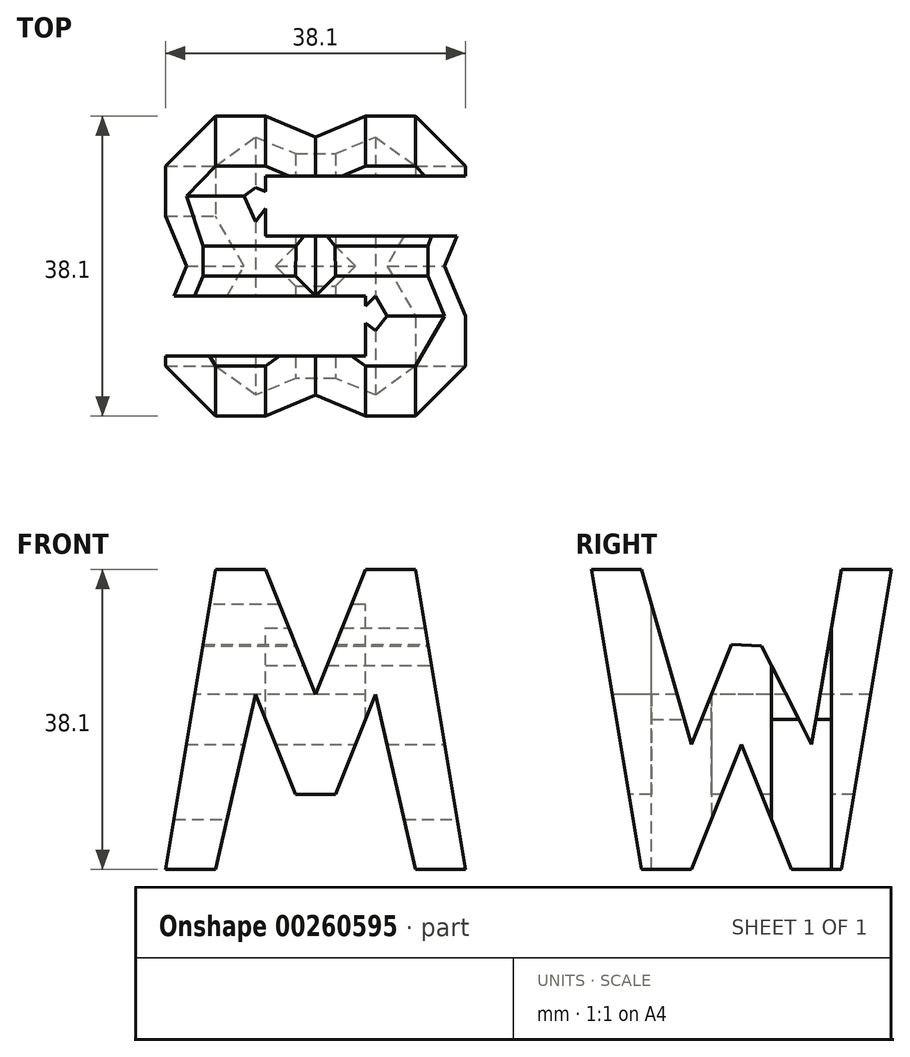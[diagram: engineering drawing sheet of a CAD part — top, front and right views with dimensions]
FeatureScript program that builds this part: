
annotation { "Feature Type Name" : "Feature", "Feature Type Description" : "" }
export const myFeature = defineFeature(function(context is Context, id is Id, definition is map)
    precondition{}
    {
        {
            var Q0;
            Q0=qCreatedBy(makeId("Front.planeOp"),FACE);
            var sketch = newSketch(context, id + "F0", { "sketchPlane" : qUnion([Q0])});
            skLineSegment(sketch, "E0", {"start": v(0, 0) * mm, "end": v(38.1, 0) * mm});
            skLineSegment(sketch, "E1", {"start": v(38.1, 0) * mm, "end": v(38.1, 38.1) * mm});
            skLineSegment(sketch, "E2", {"start": v(38.1, 38.1) * mm, "end": v(0, 38.1) * mm});
            skLineSegment(sketch, "E3", {"start": v(0, 38.1) * mm, "end": v(0, 0) * mm});
            skSolve(sketch);
        }
        {
            var Q0;
            Q0=makeQuery(id+"F0.imprint","IMPRINT",FACE,{"disambiguationData":[TD([[makeQuery(id+"F0.imprint","IMPRINT",EDGE,{"derivedFrom":sQuery(id+"F0.wireOp",EDGE,"E0")}),1.0]])]});
            extrude(context, id + "F1", {"entities" : qUnion([Q0]), "depth" : 38.1 * mm});
        }
        {
            var Q0;
            Q0=qCreatedBy(makeId("Front.planeOp"),FACE);
            cPlane(context, id + "F2", {"entities" : qUnion([Q0]), "cplaneType" : CPlaneType.OFFSET, "offset" : 38.1 * mm, "width" : 152.4 * mm, "height" : 152.4 * mm});
        }
        {
            var Q0;
            Q0=qCreatedBy(makeId("Right.planeOp"),FACE);
            cPlane(context, id + "F3", {"entities" : qUnion([Q0]), "cplaneType" : CPlaneType.OFFSET, "offset" : 38.1 * mm, "width" : 152.4 * mm, "height" : 152.4 * mm});
        }
        {
            var Q0;
            Q0=qCreatedBy(makeId("Top.planeOp"),FACE);
            cPlane(context, id + "F4", {"entities" : qUnion([Q0]), "cplaneType" : CPlaneType.OFFSET, "offset" : 38.1 * mm, "width" : 152.4 * mm, "height" : 152.4 * mm});
        }
        {
            var Q0;
            Q0=qCreatedBy(id+"F3.planeOp",FACE);
            var sketch = newSketch(context, id + "F5", { "sketchPlane" : qUnion([Q0])});
            skLineSegment(sketch, "E4", {"start": v(-38.1, 38.1) * mm, "end": v(0, 38.1) * mm});
            skLineSegment(sketch, "E5", {"start": v(0, 38.1) * mm, "end": v(0, 0) * mm});
            skLineSegment(sketch, "E6", {"start": v(0, 0) * mm, "end": v(-38.1, 0) * mm});
            skLineSegment(sketch, "E7", {"start": v(-38.1, 38.1) * mm, "end": v(-38.1, 0) * mm});
            skLineSegment(sketch, "E8", {"start": v(0, 38.1) * mm, "end": v(-6.35, 0) * mm});
            skLineSegment(sketch, "E9", {"start": v(-6.35, 0) * mm, "end": v(-12.7, 0) * mm});
            skLineSegment(sketch, "E10", {"start": v(-12.7, 0) * mm, "end": v(-19.05, 15.88) * mm});
            skLineSegment(sketch, "E11", {"start": v(-19.05, 15.87) * mm, "end": v(-25.4, 0) * mm});
            skLineSegment(sketch, "E12", {"start": v(-25.4, 0) * mm, "end": v(-31.75, 0) * mm});
            skLineSegment(sketch, "E13", {"start": v(-31.75, 0) * mm, "end": v(-38.1, 38.1) * mm});
            skLineSegment(sketch, "E14", {"start": v(-25.4, 15.87) * mm, "end": v(-31.75, 38.1) * mm});
            skPoint(sketch, "E15.end.orphan", {"position": v(-26.67, 38.1) * mm});
            skPoint(sketch, "E16.end.orphan", {"position": v(-21.59, 38.1) * mm});
            skPoint(sketch, "E17.end.orphan", {"position": v(-11.43, 38.1) * mm});
            skPoint(sketch, "E18.end.orphan", {"position": v(-16.5, 38.1) * mm});
            skPoint(sketch, "E19.end.orphan", {"position": v(-19.05, 0) * mm});
            skPoint(sketch, "E20.end.orphan", {"position": v(-12.7, 28.57) * mm});
            skPoint(sketch, "E21.start.orphan", {"position": v(-20.32, 28.57) * mm});
            skPoint(sketch, "E22.end.orphan", {"position": v(-10.16, 15.87) * mm});
            skPoint(sketch, "E22.start.orphan", {"position": v(-6.35, 38.1) * mm});
            skLineSegment(sketch, "E23", {"start": v(-10.16, 15.88) * mm, "end": v(-6.35, 38.1) * mm});
            skLineSegment(sketch, "E24", {"start": v(-21.59, 38.1) * mm, "end": v(-21.59, 28.57) * mm});
            skLineSegment(sketch, "E25", {"start": v(-16.5, 38.1) * mm, "end": v(-16.5, 28.4) * mm});
            skLineSegment(sketch, "E26", {"start": v(-16.5, 28.4) * mm, "end": v(-20.32, 28.57) * mm});
            skLineSegment(sketch, "E27", {"start": v(-10.16, 15.87) * mm, "end": v(-16.5, 28.4) * mm});
            skLineSegment(sketch, "E28", {"start": v(-16.5, 28.4) * mm, "end": v(-21.59, 28.57) * mm});
            skLineSegment(sketch, "E29", {"start": v(-25.4, 15.87) * mm, "end": v(-20.32, 28.57) * mm});
            skSolve(sketch);
        }
        {
            var Q0;
            {var subQ0=sQuery(id+"F5.wireOp",EDGE,"E7");Q0=makeQuery(id+"F5.imprint","IMPRINT",FACE,{"disambiguationData":[TD([[makeQuery(id+"F5.imprint","IMPRINT",EDGE,{"derivedFrom":subQ0}),1.0]])]});}
            var Q1;
            {var subQ0=sQuery(id+"F5.wireOp",EDGE,"E10");Q1=makeQuery(id+"F5.imprint","IMPRINT",FACE,{"disambiguationData":[TD([[makeQuery(id+"F5.imprint","IMPRINT",EDGE,{"derivedFrom":subQ0}),1.0]])]});}
            var Q2;
            {var subQ0=sQuery(id+"F5.wireOp",EDGE,"E5");Q2=makeQuery(id+"F5.imprint","IMPRINT",FACE,{"disambiguationData":[TD([[makeQuery(id+"F5.imprint","IMPRINT",EDGE,{"derivedFrom":subQ0}),-1.0]])]});}
            var Q3;
            {var subQ0=sQuery(id+"F5.wireOp",EDGE,"E23");Q3=makeQuery(id+"F5.imprint","IMPRINT",FACE,{"disambiguationData":[TD([[makeQuery(id+"F5.imprint","IMPRINT",EDGE,{"derivedFrom":subQ0}),1.0]])]});}
            var Q4;
            {var subQ4=sQuery(id+"F5.wireOp",EDGE,"E14");Q4=makeQuery(id+"F5.imprint","IMPRINT",FACE,{"disambiguationData":[TD([[makeQuery(id+"F5.imprint","IMPRINT",EDGE,{"derivedFrom":subQ4}),-1.0]])]});}
            var Q5;
            {var subQ2=sQuery(id+"F5.wireOp",EDGE,"E24");Q5=makeQuery(id+"F5.imprint","IMPRINT",FACE,{"disambiguationData":[TD([[makeQuery(id+"F5.imprint","IMPRINT",EDGE,{"derivedFrom":subQ2}),1.0]])]});}
            extrude(context, id + "F6", {"entities" : qUnion([Q0, Q1, Q2, Q3, Q4, Q5]), "operationType" : NewBodyOperationType.REMOVE, "oppositeDirection" : true, "depth" : 38.1 * mm});
        }
        {
            var Q0;
            Q0=qCreatedBy(id+"F2.planeOp",FACE);
            var sketch = newSketch(context, id + "F7", { "sketchPlane" : qUnion([Q0])});
            skLineSegment(sketch, "E30", {"start": v(0, 0) * mm, "end": v(0, 38.1) * mm});
            skLineSegment(sketch, "E31", {"start": v(0, 38.1) * mm, "end": v(38.1, 38.1) * mm});
            skLineSegment(sketch, "E32", {"start": v(38.1, 38.1) * mm, "end": v(38.1, 0) * mm});
            skLineSegment(sketch, "E33", {"start": v(38.1, 0) * mm, "end": v(0, 0) * mm});
            skLineSegment(sketch, "E34", {"start": v(0, 0) * mm, "end": v(6.35, 38.1) * mm});
            skLineSegment(sketch, "E35", {"start": v(12.7, 38.1) * mm, "end": v(19.05, 22.23) * mm});
            skLineSegment(sketch, "E36", {"start": v(19.05, 22.22) * mm, "end": v(25.4, 38.1) * mm});
            skLineSegment(sketch, "E37", {"start": v(38.1, 0) * mm, "end": v(31.75, 38.1) * mm});
            skLineSegment(sketch, "E38", {"start": v(6.35, 0) * mm, "end": v(11.43, 22.23) * mm});
            skLineSegment(sketch, "E39", {"start": v(11.43, 22.22) * mm, "end": v(16.51, 9.53) * mm});
            skLineSegment(sketch, "E40", {"start": v(16.51, 9.53) * mm, "end": v(21.6, 9.53) * mm});
            skLineSegment(sketch, "E41", {"start": v(21.6, 9.52) * mm, "end": v(26.67, 22.23) * mm});
            skLineSegment(sketch, "E42", {"start": v(26.67, 22.23) * mm, "end": v(31.75, 0) * mm});
            skPoint(sketch, "E43.end.orphan", {"position": v(19.05, 38.1) * mm});
            skPoint(sketch, "E44.end.orphan", {"position": v(11.43, 0) * mm});
            skPoint(sketch, "E45.end.orphan", {"position": v(26.67, 0) * mm});
            skSolve(sketch);
        }
        {
            var Q0;
            {var subQ0=sQuery(id+"F7.wireOp",EDGE,"E32");Q0=makeQuery(id+"F7.imprint","IMPRINT",FACE,{"disambiguationData":[TD([[makeQuery(id+"F7.imprint","IMPRINT",EDGE,{"derivedFrom":subQ0}),-1.0]])]});}
            var Q1;
            {var subQ0=sQuery(id+"F7.wireOp",EDGE,"E35");Q1=makeQuery(id+"F7.imprint","IMPRINT",FACE,{"disambiguationData":[TD([[makeQuery(id+"F7.imprint","IMPRINT",EDGE,{"derivedFrom":subQ0}),1.0]])]});}
            var Q2;
            {var subQ0=sQuery(id+"F7.wireOp",EDGE,"E30");Q2=makeQuery(id+"F7.imprint","IMPRINT",FACE,{"disambiguationData":[TD([[makeQuery(id+"F7.imprint","IMPRINT",EDGE,{"derivedFrom":subQ0}),-1.0]])]});}
            var Q3;
            {var subQ1=sQuery(id+"F7.wireOp",EDGE,"E38");Q3=makeQuery(id+"F7.imprint","IMPRINT",FACE,{"disambiguationData":[TD([[makeQuery(id+"F7.imprint","IMPRINT",EDGE,{"derivedFrom":subQ1}),-1.0]])]});}
            extrude(context, id + "F8", {"entities" : qUnion([Q0, Q1, Q2, Q3]), "operationType" : NewBodyOperationType.REMOVE, "oppositeDirection" : true, "depth" : 38.1 * mm});
        }
        {
            var Q0;
            Q0=qCreatedBy(id+"F4.planeOp",FACE);
            var sketch = newSketch(context, id + "F9", { "sketchPlane" : qUnion([Q0])});
            skLineSegment(sketch, "E46", {"start": v(0, 0) * mm, "end": v(38.1, 0) * mm});
            skLineSegment(sketch, "E47", {"start": v(38.1, 0) * mm, "end": v(38.1, -38.1) * mm});
            skLineSegment(sketch, "E48", {"start": v(38.1, -38.1) * mm, "end": v(0, -38.1) * mm});
            skLineSegment(sketch, "E49", {"start": v(0, -38.1) * mm, "end": v(0, 0) * mm});
            skLineSegment(sketch, "E50", {"start": v(38.1, -7.62) * mm, "end": v(12.7, -7.62) * mm});
            skLineSegment(sketch, "E51", {"start": v(12.7, -7.62) * mm, "end": v(12.7, -15.24) * mm});
            skLineSegment(sketch, "E52", {"start": v(12.7, -15.24) * mm, "end": v(38.1, -15.24) * mm});
            skLineSegment(sketch, "E53", {"start": v(0, -22.86) * mm, "end": v(25.4, -22.86) * mm});
            skLineSegment(sketch, "E54", {"start": v(25.4, -22.86) * mm, "end": v(25.4, -30.48) * mm});
            skLineSegment(sketch, "E55", {"start": v(25.4, -30.48) * mm, "end": v(0, -30.48) * mm});
            skSolve(sketch);
        }
        {
            var Q0;
            {var subQ0=sQuery(id+"F9.wireOp",EDGE,"E50");Q0=makeQuery(id+"F9.imprint","IMPRINT",FACE,{"disambiguationData":[TD([[makeQuery(id+"F9.imprint","IMPRINT",EDGE,{"derivedFrom":subQ0}),1.0]])]});}
            var Q1;
            {var subQ0=sQuery(id+"F9.wireOp",EDGE,"E53");Q1=makeQuery(id+"F9.imprint","IMPRINT",FACE,{"disambiguationData":[TD([[makeQuery(id+"F9.imprint","IMPRINT",EDGE,{"derivedFrom":subQ0}),-1.0]])]});}
            extrude(context, id + "F10", {"entities" : qUnion([Q0, Q1]), "operationType" : NewBodyOperationType.REMOVE, "oppositeDirection" : true, "depth" : 38.1 * mm});
        }
    });
